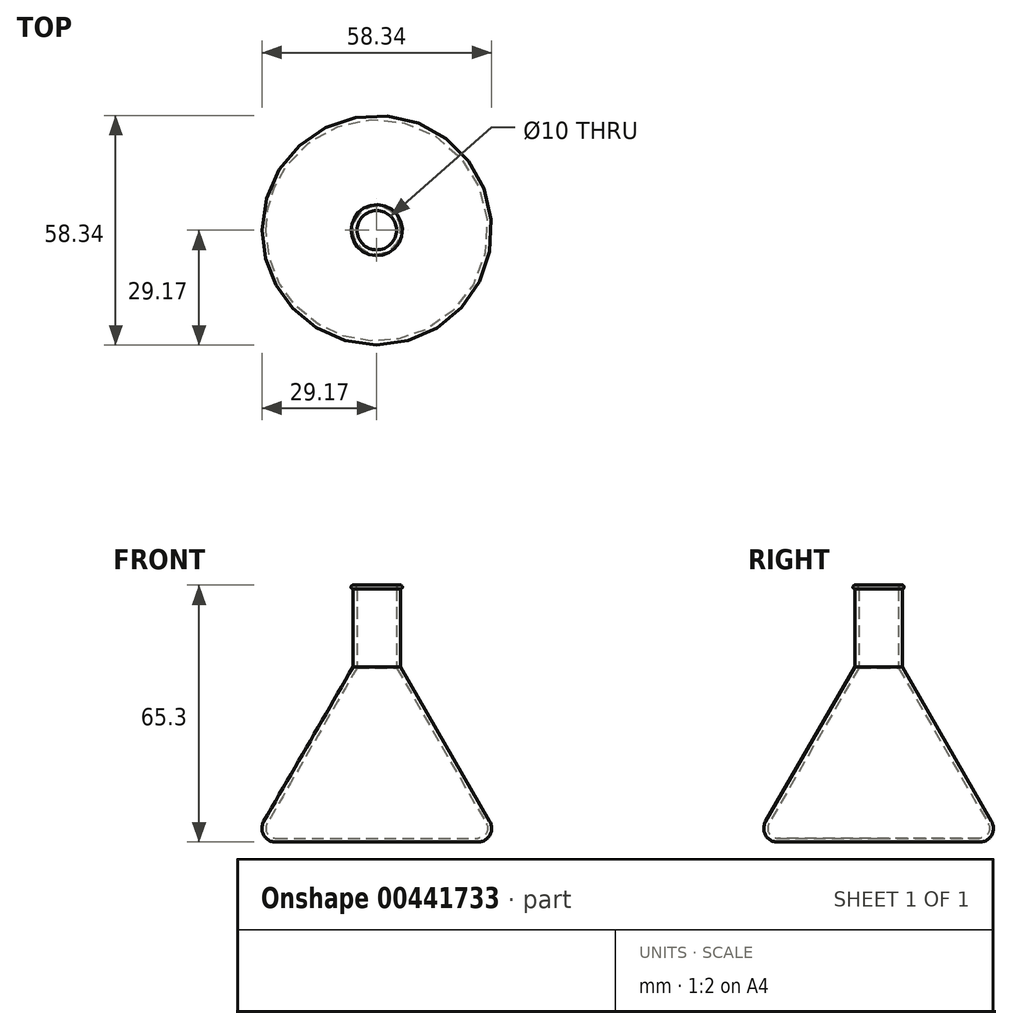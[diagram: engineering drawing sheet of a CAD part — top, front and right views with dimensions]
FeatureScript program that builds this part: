
annotation { "Feature Type Name" : "Feature", "Feature Type Description" : "" }
export const myFeature = defineFeature(function(context is Context, id is Id, definition is map)
    precondition{}
    {
        {
            var Q0;
            Q0=qCreatedBy(makeId("Front.planeOp"),FACE);
            var sketch = newSketch(context, id + "F0", { "sketchPlane" : qUnion([Q0])});
            skLineSegment(sketch, "E0", {"start": v(-5, 63.3) * mm, "end": v(-5, 43.3) * mm});
            skLineSegment(sketch, "E1", {"start": v(-5, 43.3) * mm, "end": v(-27.83, 3.75) * mm});
            skLineSegment(sketch, "E2", {"start": v(-25.67, 0) * mm, "end": v(0, 0) * mm});
            skLineSegment(sketch, "E3", {"start": v(0, 0) * mm, "end": v(0, 63.3) * mm});
            skPoint(sketch, "E4.visualSharp", {"position": v(-30, 0) * mm});
            skArc(sketch, "E4.filletArc", {"start": v(-27.83, 3.75) * mm, "mid": v(-27.83, 1.25) * mm, "end": v(-25.67, 0) * mm});
            skLineSegment(sketch, "E5.0", {"start": v(-25.67, -1) * mm, "end": v(0, -1) * mm});
            skArc(sketch, "E5.1", {"start": v(-28.7, 4.25) * mm, "mid": v(-28.7, 0.75) * mm, "end": v(-25.67, -1) * mm});
            skLineSegment(sketch, "E5.2", {"start": v(-6, 43.57) * mm, "end": v(-28.7, 4.25) * mm});
            skLineSegment(sketch, "E5.3", {"start": v(-6, 63.3) * mm, "end": v(-6, 43.57) * mm});
            skLineSegment(sketch, "E6", {"start": v(0, 0) * mm, "end": v(0, -1) * mm});
            skLineSegment(sketch, "E7", {"start": v(-5, 63.3) * mm, "end": v(-5, 64.3) * mm});
            skLineSegment(sketch, "E8", {"start": v(-5, 64.3) * mm, "end": v(-6, 64.3) * mm});
            skArc(sketch, "E9", {"start": v(-6, 64.3) * mm, "mid": v(-6.5, 63.8) * mm, "end": v(-6, 63.3) * mm});
            skSolve(sketch);
        }
        {
            var Q0;
            Q0=makeQuery(id+"F0.imprint","IMPRINT",FACE,{"disambiguationData":[TD([[makeQuery(id+"F0.imprint","IMPRINT",EDGE,{"derivedFrom":sQuery(id+"F0.wireOp",EDGE,"E0")}),-1.0]])]});
            var Q1;
            Q1=sQuery(id+"F0.wireOp",EDGE,"E3");
            revolve(context, id + "F1", {"entities" : qUnion([Q0]), "axis" : qUnion([Q1]), "revolveType" : RevolveType.FULL});
        }
        {
            var Q0;
            Q0=makeQuery(id+"F1.opRevolve","SWEPT_EDGE",EDGE,{"disambiguationData":[OSD([sQuery(id+"F0.wireOp",EDGE,"E7"),sQuery(id+"F0.wireOp",EDGE,"E8")])]});
            fillet(context, id + "F2", {"entities" : qUnion([Q0]), "radius" : 1 * mm, "tangentPropagation" : true, "allowEdgeOverflow" : false});
        }
    });
